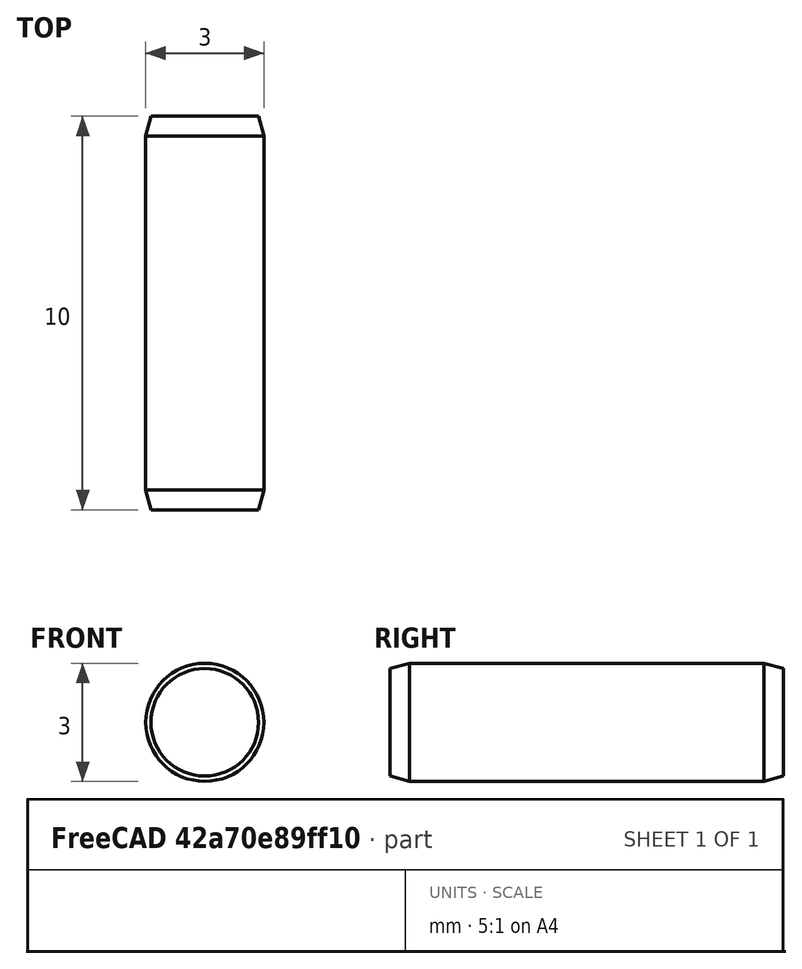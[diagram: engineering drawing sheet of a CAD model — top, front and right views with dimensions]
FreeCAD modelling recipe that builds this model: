
FCSTD DOCUMENT  (FreeCAD 0.15R4470 (Git))
Label: Zyl-Stift_ISO_8734-3x10
License: CC-BY 3.0
LicenseURL: http://creativecommons.org/licenses/by/3.0/
objects: Sketcher::SketchObject×1, PartDesign::Revolution×1
note: 3 computed .brp shape members not serialized (recipe doc carries the construction recipe); baked Part::Feature solids carry a one-line shape summary decoded from their .brp

FEATURE [Sketcher::SketchObject] Sketch
  Placement = pos=(0,0,0) rot=(0.57735,0.57735,0.57735;2.0944rad)
  sketch-geometry (7):
    g0: LineSegment StartX=0 StartY=0 StartZ=0 EndX=0 EndY=1.36603 EndZ=0
    g1: LineSegment StartX=0 StartY=1.36603 StartZ=0 EndX=0.5 EndY=1.5 EndZ=0
    g2: LineSegment StartX=0.5 StartY=1.5 StartZ=0 EndX=9.5 EndY=1.5 EndZ=0
    g3: LineSegment StartX=9.5 StartY=1.5 StartZ=0 EndX=10 EndY=1.36603 EndZ=0
    g4: LineSegment StartX=10 StartY=1.36603 StartZ=0 EndX=10 EndY=0 EndZ=0
    g5: LineSegment StartX=10 StartY=0 StartZ=0 EndX=0 EndY=0 EndZ=0
    g6: LineSegment [constr] StartX=0 StartY=1.36603 StartZ=0 EndX=10 EndY=1.36603 EndZ=0
  constraints (19):
    c: Coincident(g0,g-1)
    c: PointOnObject(g0,g-2)
    c: Coincident(g0,g1)
    c: Coincident(g1,g2)
    c: Horizontal(g2)
    c: Coincident(g2,g3)
    c: Coincident(g3,g4)
    c: Vertical(g4)
    c: Coincident(g4,g5)
    c: Coincident(g5,g-1)
    c: Horizontal(g5)
    c: Equal(g3,g1)
    c: Coincident(g6,g0)
    c: Coincident(g6,g3)
    c: Horizontal(g6)
    c: Angle(g6,g1) = 0.261799
    c: DistanceY(g-1,g1) = 1.5
    c: DistanceX(g5) = -10
    c: DistanceX(g1) = 0.5
FEATURE [PartDesign::Revolution] Revolution  label="Zyl-Stift ISO 8734-3x10 #"
  Angle = 360
  Axis = (0,1,0)
  Base = (0,0,0)
  Placement = pos=(0,0,0) rot=(0.57735,0.57735,0.57735;2.0944rad)
  ReferenceAxis = -> Sketch [H_Axis]
  Sketch = -> Sketch
